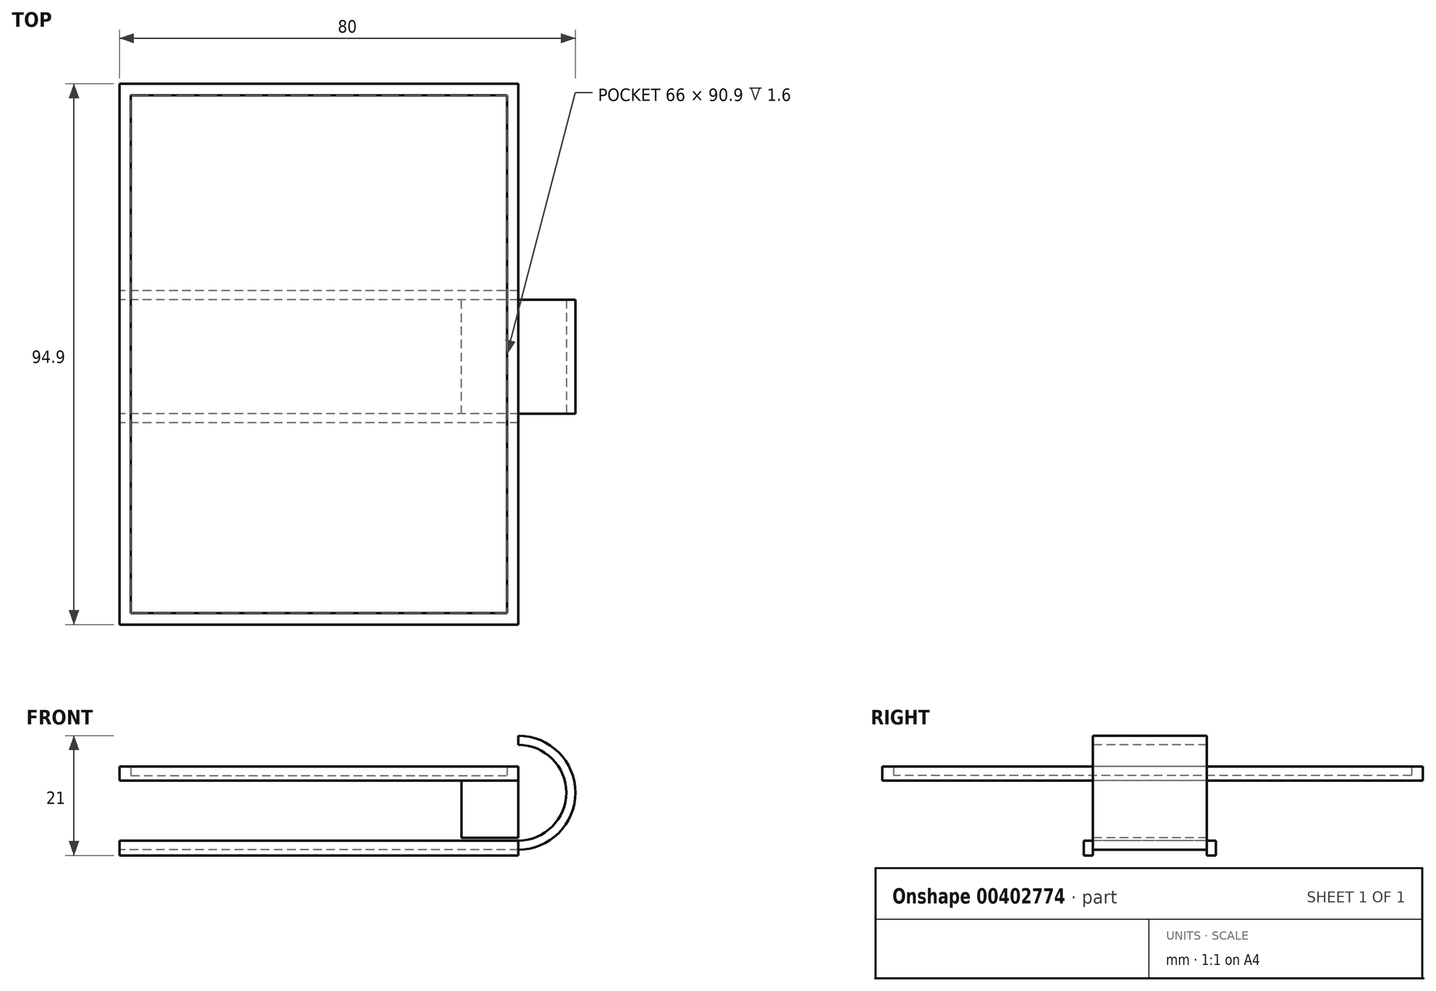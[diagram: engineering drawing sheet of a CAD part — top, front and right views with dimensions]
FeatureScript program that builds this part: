
annotation { "Feature Type Name" : "Feature", "Feature Type Description" : "" }
export const myFeature = defineFeature(function(context is Context, id is Id, definition is map)
    precondition{}
    {
        {
            var Q0;
            Q0=qCreatedBy(makeId("Top.planeOp"),FACE);
            var sketch = newSketch(context, id + "F0", { "sketchPlane" : qUnion([Q0])});
            skLineSegment(sketch, "E0.bottom", {"start": v(-31.17, 45.45) * mm, "end": v(34.83, 45.45) * mm});
            skLineSegment(sketch, "E0.top", {"start": v(-31.17, -45.45) * mm, "end": v(34.83, -45.45) * mm});
            skLineSegment(sketch, "E0.left", {"start": v(-31.17, 45.45) * mm, "end": v(-31.17, -45.45) * mm});
            skLineSegment(sketch, "E0.right", {"start": v(34.83, 45.45) * mm, "end": v(34.83, -45.45) * mm});
            skPoint(sketch, "E0.middle", {"position": v(1.83, 0) * mm});
            skLineSegment(sketch, "E1.0", {"start": v(-33.17, 47.45) * mm, "end": v(36.83, 47.45) * mm});
            skLineSegment(sketch, "E1.1", {"start": v(-33.17, 47.45) * mm, "end": v(-33.17, -47.45) * mm});
            skLineSegment(sketch, "E1.2", {"start": v(-33.17, -47.45) * mm, "end": v(36.83, -47.45) * mm});
            skLineSegment(sketch, "E1.3", {"start": v(36.83, 47.45) * mm, "end": v(36.83, -47.45) * mm});
            skSolve(sketch);
        }
        {
            var Q0;
            Q0=makeQuery(id+"F0.imprint","IMPRINT",FACE,{"disambiguationData":[TD([[makeQuery(id+"F0.imprint","IMPRINT",EDGE,{"derivedFrom":sQuery(id+"F0.wireOp",EDGE,"E0.bottom")}),-1.0]])]});
            var Q1;
            Q1=makeQuery(id+"F0.imprint","IMPRINT",FACE,{"disambiguationData":[TD([[makeQuery(id+"F0.imprint","IMPRINT",EDGE,{"derivedFrom":sQuery(id+"F0.wireOp",EDGE,"E0.bottom")}),1.0]])]});
            extrude(context, id + "F1", {"entities" : qUnion([Q0, Q1]), "depth" : 0.9 * mm});
        }
        {
            var Q0;
            Q0=makeQuery(id+"F1.opExtrude","CAP_FACE",FACE,{"disambiguationData":[OSD([sQuery(id+"F0.wireOp",EDGE,"E1.0"),sQuery(id+"F0.wireOp",EDGE,"E1.1"),sQuery(id+"F0.wireOp",EDGE,"E1.2"),sQuery(id+"F0.wireOp",EDGE,"E1.3")])],"isStart":false});
            var sketch = newSketch(context, id + "F2", { "sketchPlane" : qUnion([Q0])});
            skLineSegment(sketch, "E2.0", {"start": v(-31.17, 45.45) * mm, "end": v(34.83, 45.45) * mm});
            skLineSegment(sketch, "E2.1", {"start": v(-31.17, 45.45) * mm, "end": v(-31.17, -45.45) * mm});
            skLineSegment(sketch, "E2.2", {"start": v(-31.17, -45.45) * mm, "end": v(34.83, -45.45) * mm});
            skLineSegment(sketch, "E2.3", {"start": v(34.83, 45.45) * mm, "end": v(34.83, -45.45) * mm});
            skSolve(sketch);
        }
        {
            var Q0;
            Q0=makeQuery(id+"F2.imprint","IMPRINT",FACE,{"disambiguationData":[TD([[makeQuery(id+"F2.imprint","IMPRINT",EDGE,{"derivedFrom":sQuery(id+"F2.wireOp",EDGE,"E2.0")}),1.0]])]});
            extrude(context, id + "F3", {"entities" : qUnion([Q0]), "operationType" : NewBodyOperationType.ADD, "depth" : 1.6 * mm});
        }
        {
            var Q0;
            Q0=makeQuery(id+"F1.opExtrude","CAP_FACE",FACE,{"disambiguationData":[OSD([sQuery(id+"F0.wireOp",EDGE,"E1.0"),sQuery(id+"F0.wireOp",EDGE,"E1.1"),sQuery(id+"F0.wireOp",EDGE,"E1.2"),sQuery(id+"F0.wireOp",EDGE,"E1.3")])],"isStart":true});
            var sketch = newSketch(context, id + "F4", { "sketchPlane" : qUnion([Q0])});
            skLineSegment(sketch, "E3.bottom", {"start": v(36.83, 10.45) * mm, "end": v(26.83, 10.45) * mm});
            skLineSegment(sketch, "E3.top", {"start": v(36.83, -9.55) * mm, "end": v(26.83, -9.55) * mm});
            skLineSegment(sketch, "E3.left", {"start": v(36.83, 10.45) * mm, "end": v(36.83, -9.55) * mm});
            skLineSegment(sketch, "E3.right", {"start": v(26.83, 10.45) * mm, "end": v(26.83, -9.55) * mm});
            skSolve(sketch);
        }
        {
            var Q0;
            Q0 = qSketchRegion(id + "F4", true);
            extrude(context, id + "F5", {"entities" : qUnion([Q0]), "depth" : 10 * mm});
        }
        {
            var Q0;
            Q0=makeQuery(id+"F5.opExtrude","SWEPT_FACE",FACE,{"disambiguationData":[OSD([sQuery(id+"F4.wireOp",EDGE,"E3.bottom")])]});
            var sketch = newSketch(context, id + "F6", { "sketchPlane" : qUnion([Q0])});
            skLineSegment(sketch, "E4.0.1", {"start": v(34.83, 0.9) * mm, "end": v(34.83, 2.5) * mm});
            skLineSegment(sketch, "E4.0.3", {"start": v(34.83, 2.5) * mm, "end": v(34.83, 0.9) * mm});
            skLineSegment(sketch, "E5", {"start": v(34.83, 0.9) * mm, "end": v(34.83, 7.9) * mm});
            skArc(sketch, "E6", {"start": v(36.83, -12.09) * mm, "mid": v(46.83, -2.09) * mm, "end": v(36.83, 7.91) * mm});
            skLineSegment(sketch, "E7", {"start": v(36.83, -12.09) * mm, "end": v(36.83, 7.91) * mm});
            skPoint(sketch, "E8.end.orphan", {"position": v(36.83, 7.9) * mm});
            skLineSegment(sketch, "E9", {"start": v(36.83, -12.09) * mm, "end": v(-33.17, -12.09) * mm});
            skArc(sketch, "E10.0", {"start": v(36.83, -10.49) * mm, "mid": v(45.23, -2.09) * mm, "end": v(36.83, 6.31) * mm});
            skLineSegment(sketch, "E10.1", {"start": v(36.83, -10.49) * mm, "end": v(-33.17, -10.49) * mm});
            skLineSegment(sketch, "E11", {"start": v(-33.17, -10.49) * mm, "end": v(-33.17, -12.09) * mm});
            skLineSegment(sketch, "E12", {"start": v(36.83, 6.31) * mm, "end": v(36.83, 7.91) * mm});
            skSolve(sketch);
        }
        {
            var Q0;
            {var subQ0=sQuery(id+"F6.wireOp",EDGE,"E9");Q0=makeQuery(id+"F6.imprint","IMPRINT",FACE,{"disambiguationData":[TD([[makeQuery(id+"F6.imprint","IMPRINT",EDGE,{"derivedFrom":subQ0}),-1.0]])]});}
            var Q1;
            {var subQ0=sQuery(id+"F6.wireOp",EDGE,"E6");Q1=makeQuery(id+"F6.imprint","IMPRINT",FACE,{"disambiguationData":[TD([[makeQuery(id+"F6.imprint","IMPRINT",EDGE,{"derivedFrom":subQ0}),1.0]])]});}
            extrude(context, id + "F7", {"entities" : qUnion([Q0, Q1]), "oppositeDirection" : true, "depth" : 20 * mm});
        }
        {
            var Q0;
            Q0=makeQuery(id+"F7.opExtrude","CAP_FACE",FACE,{"disambiguationData":[OSD([sQuery(id+"F6.wireOp",EDGE,"E6"),sQuery(id+"F6.wireOp",EDGE,"E9"),sQuery(id+"F6.wireOp",EDGE,"E10.0"),sQuery(id+"F6.wireOp",EDGE,"E10.1"),sQuery(id+"F6.wireOp",EDGE,"E11"),sQuery(id+"F6.wireOp",EDGE,"E12")])],"isStart":true});
            var sketch = newSketch(context, id + "F8", { "sketchPlane" : qUnion([Q0])});
            skLineSegment(sketch, "E13.bottom", {"start": v(-33.17, -10.49) * mm, "end": v(36.83, -10.49) * mm});
            skLineSegment(sketch, "E13.top", {"start": v(-33.17, -13.09) * mm, "end": v(36.83, -13.09) * mm});
            skLineSegment(sketch, "E13.left", {"start": v(-33.17, -10.49) * mm, "end": v(-33.17, -13.09) * mm});
            skLineSegment(sketch, "E13.right", {"start": v(36.83, -10.49) * mm, "end": v(36.83, -13.09) * mm});
            skSolve(sketch);
        }
        {
            var Q0;
            Q0 = qSketchRegion(id + "F8", true);
            extrude(context, id + "F9", {"entities" : qUnion([Q0]), "operationType" : NewBodyOperationType.ADD, "depth" : 1.6 * mm});
        }
        {
            var Q0;
            Q0=makeQuery(id+"F7.opExtrude","CAP_FACE",FACE,{"disambiguationData":[OSD([sQuery(id+"F6.wireOp",EDGE,"E6"),sQuery(id+"F6.wireOp",EDGE,"E9"),sQuery(id+"F6.wireOp",EDGE,"E10.0"),sQuery(id+"F6.wireOp",EDGE,"E10.1"),sQuery(id+"F6.wireOp",EDGE,"E11"),sQuery(id+"F6.wireOp",EDGE,"E12")])],"isStart":false});
            var sketch = newSketch(context, id + "F10", { "sketchPlane" : qUnion([Q0])});
            skLineSegment(sketch, "E14.bottom", {"start": v(33.17, -10.49) * mm, "end": v(-36.83, -10.49) * mm});
            skLineSegment(sketch, "E14.top", {"start": v(33.17, -13.09) * mm, "end": v(-36.83, -13.09) * mm});
            skLineSegment(sketch, "E14.left", {"start": v(33.17, -10.49) * mm, "end": v(33.17, -13.09) * mm});
            skLineSegment(sketch, "E14.right", {"start": v(-36.83, -10.49) * mm, "end": v(-36.83, -13.09) * mm});
            skSolve(sketch);
        }
        {
            var Q0;
            Q0 = qSketchRegion(id + "F10", true);
            extrude(context, id + "F11", {"entities" : qUnion([Q0]), "operationType" : NewBodyOperationType.ADD, "depth" : 1.6 * mm});
        }
    });
